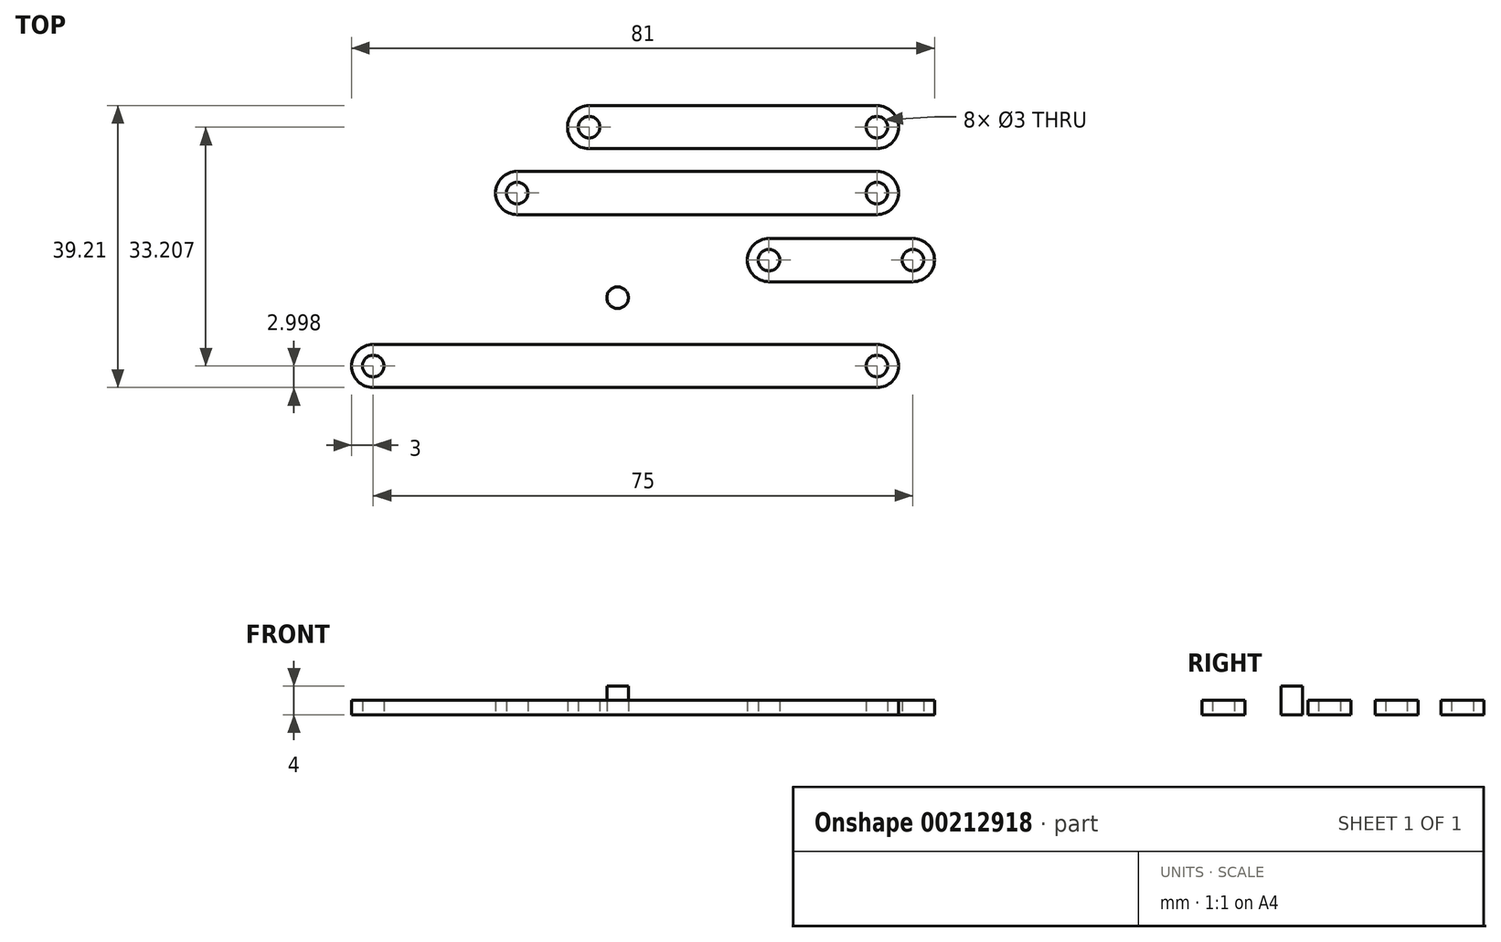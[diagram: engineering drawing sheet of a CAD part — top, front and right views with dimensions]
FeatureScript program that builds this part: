
annotation { "Feature Type Name" : "Feature", "Feature Type Description" : "" }
export const myFeature = defineFeature(function(context is Context, id is Id, definition is map)
    precondition{}
    {
        {
            var Q0;
            Q0=qCreatedBy(makeId("Top.planeOp"),FACE);
            var sketch = newSketch(context, id + "F0", { "sketchPlane" : qUnion([Q0])});
            skCircle(sketch, "E0", {"center": v(0, 0) * mm, "radius": 1.5 * mm});
            skCircle(sketch, "E1", {"center": v(20, 0) * mm, "radius": 1.5 * mm});
            skPoint(sketch, "E2", {"position": v(0, 3) * mm});
            skPoint(sketch, "E3", {"position": v(0, -3) * mm});
            skArc(sketch, "E4", {"start": v(0, 3) * mm, "mid": v(-3, 0) * mm, "end": v(0, -3) * mm});
            skPoint(sketch, "E5", {"position": v(20, 3) * mm});
            skPoint(sketch, "E6", {"position": v(20, -3) * mm});
            skArc(sketch, "E7", {"start": v(20, 3) * mm, "mid": v(23, 0) * mm, "end": v(20, -3) * mm});
            skLineSegment(sketch, "E8", {"start": v(0, 3) * mm, "end": v(20, 3) * mm});
            skLineSegment(sketch, "E9", {"start": v(0, -3) * mm, "end": v(20, -3) * mm});
            skSolve(sketch);
        }
        {
            var Q0;
            Q0 = qSketchRegion(id + "F0", true);
            extrude(context, id + "F1", {"entities" : qUnion([Q0]), "depth" : 2 * mm});
        }
        {
            var Q0;
            Q0=qCreatedBy(makeId("Top.planeOp"),FACE);
            var sketch = newSketch(context, id + "F2", { "sketchPlane" : qUnion([Q0])});
            skCircle(sketch, "E10", {"center": v(-25, 18.49) * mm, "radius": 1.5 * mm});
            skCircle(sketch, "E11", {"center": v(15, 18.49) * mm, "radius": 1.5 * mm});
            skPoint(sketch, "E12", {"position": v(-25, 21.49) * mm});
            skPoint(sketch, "E13", {"position": v(-25, 15.49) * mm});
            skArc(sketch, "E14", {"start": v(-25, 21.49) * mm, "mid": v(-28, 18.49) * mm, "end": v(-25, 15.49) * mm});
            skPoint(sketch, "E15", {"position": v(15, 21.49) * mm});
            skPoint(sketch, "E16", {"position": v(15, 15.49) * mm});
            skArc(sketch, "E17", {"start": v(15, 21.49) * mm, "mid": v(18, 18.49) * mm, "end": v(15, 15.49) * mm});
            skLineSegment(sketch, "E18", {"start": v(-25, 21.49) * mm, "end": v(15, 21.49) * mm});
            skLineSegment(sketch, "E19", {"start": v(-25, 15.49) * mm, "end": v(15, 15.49) * mm});
            skSolve(sketch);
        }
        {
            var Q0;
            Q0 = qSketchRegion(id + "F2", true);
            extrude(context, id + "F3", {"entities" : qUnion([Q0]), "depth" : 2 * mm});
        }
        {
            var Q0;
            Q0=qCreatedBy(makeId("Top.planeOp"),FACE);
            var sketch = newSketch(context, id + "F4", { "sketchPlane" : qUnion([Q0])});
            skCircle(sketch, "E20", {"center": v(-55, -14.72) * mm, "radius": 1.5 * mm});
            skCircle(sketch, "E21", {"center": v(15, -14.72) * mm, "radius": 1.5 * mm});
            skPoint(sketch, "E22", {"position": v(-55, -11.72) * mm});
            skPoint(sketch, "E23", {"position": v(-55, -17.72) * mm});
            skArc(sketch, "E24", {"start": v(-55, -11.72) * mm, "mid": v(-58, -14.72) * mm, "end": v(-55, -17.72) * mm});
            skPoint(sketch, "E25", {"position": v(15, -11.72) * mm});
            skPoint(sketch, "E26", {"position": v(15, -17.72) * mm});
            skArc(sketch, "E27", {"start": v(15, -11.72) * mm, "mid": v(18, -14.72) * mm, "end": v(15, -17.72) * mm});
            skLineSegment(sketch, "E28", {"start": v(-55, -11.72) * mm, "end": v(15, -11.72) * mm});
            skLineSegment(sketch, "E29", {"start": v(-55, -17.72) * mm, "end": v(15, -17.72) * mm});
            skSolve(sketch);
        }
        {
            var Q0;
            Q0 = qSketchRegion(id + "F4", true);
            extrude(context, id + "F5", {"entities" : qUnion([Q0]), "depth" : 2 * mm});
        }
        {
            var Q0;
            Q0=qCreatedBy(makeId("Top.planeOp"),FACE);
            var sketch = newSketch(context, id + "F6", { "sketchPlane" : qUnion([Q0])});
            skCircle(sketch, "E30", {"center": v(-35, 9.33) * mm, "radius": 1.5 * mm});
            skCircle(sketch, "E31", {"center": v(15, 9.33) * mm, "radius": 1.5 * mm});
            skPoint(sketch, "E32", {"position": v(-35, 12.33) * mm});
            skPoint(sketch, "E33", {"position": v(-35, 6.33) * mm});
            skArc(sketch, "E34", {"start": v(-35, 12.33) * mm, "mid": v(-38, 9.33) * mm, "end": v(-35, 6.33) * mm});
            skPoint(sketch, "E35", {"position": v(15, 12.33) * mm});
            skPoint(sketch, "E36", {"position": v(15, 6.33) * mm});
            skArc(sketch, "E37", {"start": v(15, 12.33) * mm, "mid": v(18, 9.33) * mm, "end": v(15, 6.33) * mm});
            skLineSegment(sketch, "E38", {"start": v(-35, 12.33) * mm, "end": v(15, 12.33) * mm});
            skLineSegment(sketch, "E39", {"start": v(-35, 6.33) * mm, "end": v(15, 6.33) * mm});
            skSolve(sketch);
        }
        {
            var Q0;
            Q0 = qSketchRegion(id + "F6", true);
            extrude(context, id + "F7", {"entities" : qUnion([Q0]), "depth" : 2 * mm});
        }
        {
            var Q0;
            Q0=qCreatedBy(makeId("Top.planeOp"),FACE);
            var sketch = newSketch(context, id + "F8", { "sketchPlane" : qUnion([Q0])});
            skCircle(sketch, "E40", {"center": v(-21.03, -5.23) * mm, "radius": 1.5 * mm});
            skSolve(sketch);
        }
        {
            var Q0;
            Q0 = qSketchRegion(id + "F8", true);
            extrude(context, id + "F9", {"entities" : qUnion([Q0]), "operationType" : NewBodyOperationType.ADD, "depth" : 4 * mm});
        }
    });
